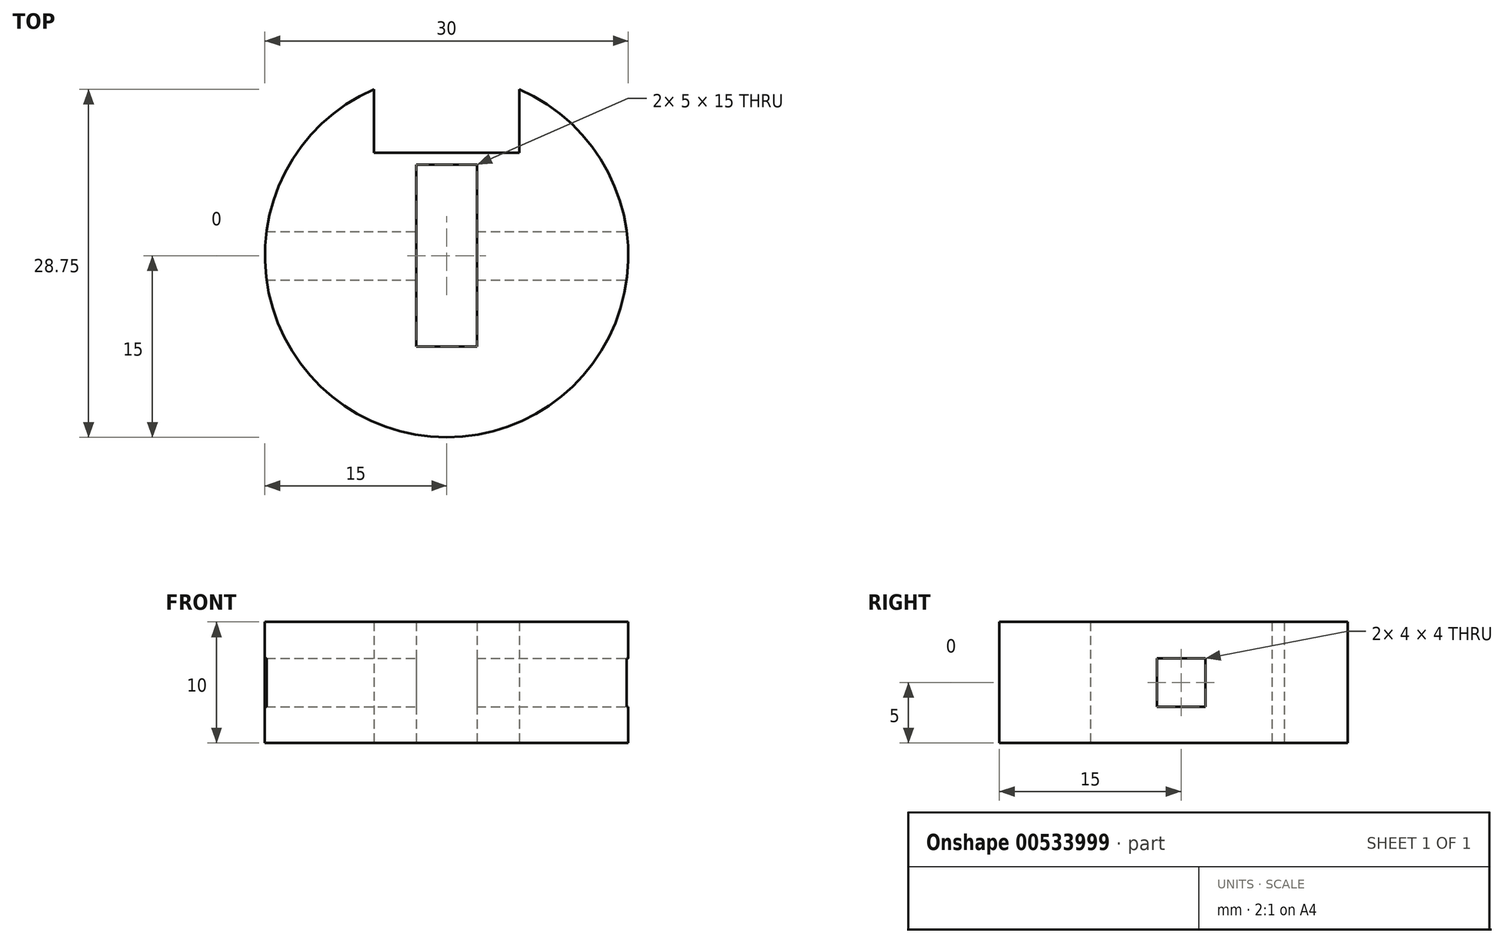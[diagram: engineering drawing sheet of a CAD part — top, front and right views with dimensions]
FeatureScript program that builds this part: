
annotation { "Feature Type Name" : "Feature", "Feature Type Description" : "" }
export const myFeature = defineFeature(function(context is Context, id is Id, definition is map)
    precondition{}
    {
        {
            var Q0;
            Q0=qCreatedBy(makeId("Top.planeOp"),FACE);
            var sketch = newSketch(context, id + "F0", { "sketchPlane" : qUnion([Q0])});
            skCircle(sketch, "E0", {"center": v(0, 0) * mm, "radius": 15 * mm});
            skLineSegment(sketch, "E1", {"start": v(0, 15) * mm, "end": v(0, -15) * mm});
            skLineSegment(sketch, "E2.bottom", {"start": v(2.5, 7.5) * mm, "end": v(-2.5, 7.5) * mm});
            skLineSegment(sketch, "E2.top", {"start": v(2.5, -7.5) * mm, "end": v(-2.5, -7.5) * mm});
            skLineSegment(sketch, "E2.left", {"start": v(2.5, 7.5) * mm, "end": v(2.5, -7.5) * mm});
            skLineSegment(sketch, "E2.right", {"start": v(-2.5, 7.5) * mm, "end": v(-2.5, -7.5) * mm});
            skLineSegment(sketch, "E3.bottom", {"start": v(6, 15.5) * mm, "end": v(-6, 15.5) * mm});
            skLineSegment(sketch, "E3.top", {"start": v(6, 8.5) * mm, "end": v(-6, 8.5) * mm});
            skLineSegment(sketch, "E3.left", {"start": v(6, 15.5) * mm, "end": v(6, 8.5) * mm});
            skLineSegment(sketch, "E3.right", {"start": v(-6, 15.5) * mm, "end": v(-6, 8.5) * mm});
            skPoint(sketch, "E3.middle", {"position": v(0, 12) * mm});
            skSolve(sketch);
        }
        {
            var Q0;
            {var subQ0=sQuery(id+"F0.wireOp",EDGE,"E2.right");Q0=makeQuery(id+"F0.imprint","IMPRINT",FACE,{"disambiguationData":[TD([[makeQuery(id+"F0.imprint","IMPRINT",EDGE,{"derivedFrom":subQ0}),-1.0]])]});}
            var Q1;
            {var subQ12=sQuery(id+"F0.wireOp",EDGE,"E2.left");Q1=makeQuery(id+"F0.imprint","IMPRINT",FACE,{"disambiguationData":[TD([[makeQuery(id+"F0.imprint","IMPRINT",EDGE,{"derivedFrom":subQ12}),1.0]])]});}
            extrude(context, id + "F1", {"entities" : qUnion([Q0, Q1]), "depth" : 5 * mm, "offsetDistance" : 25 * mm, "hasSecondDirection" : true, "secondDirectionOppositeDirection" : true, "secondDirectionDepth" : 5 * mm});
        }
        {
            var Q0;
            Q0=qCreatedBy(makeId("Right.planeOp"),FACE);
            var sketch = newSketch(context, id + "F2", { "sketchPlane" : qUnion([Q0])});
            skLineSegment(sketch, "E4.bottom", {"start": v(2, 2) * mm, "end": v(-2, 2) * mm});
            skLineSegment(sketch, "E4.top", {"start": v(2, -2) * mm, "end": v(-2, -2) * mm});
            skLineSegment(sketch, "E4.left", {"start": v(2, 2) * mm, "end": v(2, -2) * mm});
            skLineSegment(sketch, "E4.right", {"start": v(-2, 2) * mm, "end": v(-2, -2) * mm});
            skPoint(sketch, "E4.middle", {"position": v(0, 0) * mm});
            skSolve(sketch);
        }
        {
            var Q0;
            Q0=makeQuery(id+"F2.imprint","IMPRINT",FACE,{"disambiguationData":[TD([[makeQuery(id+"F2.imprint","IMPRINT",EDGE,{"derivedFrom":sQuery(id+"F2.wireOp",EDGE,"E4.bottom")}),1.0]])]});
            extrude(context, id + "F3", {"entities" : qUnion([Q0]), "operationType" : NewBodyOperationType.REMOVE, "oppositeDirection" : true, "depth" : 25 * mm, "offsetDistance" : 25 * mm, "hasSecondDirection" : true, "secondDirectionOppositeDirection" : false, "secondDirectionDepth" : 25 * mm});
        }
    });
